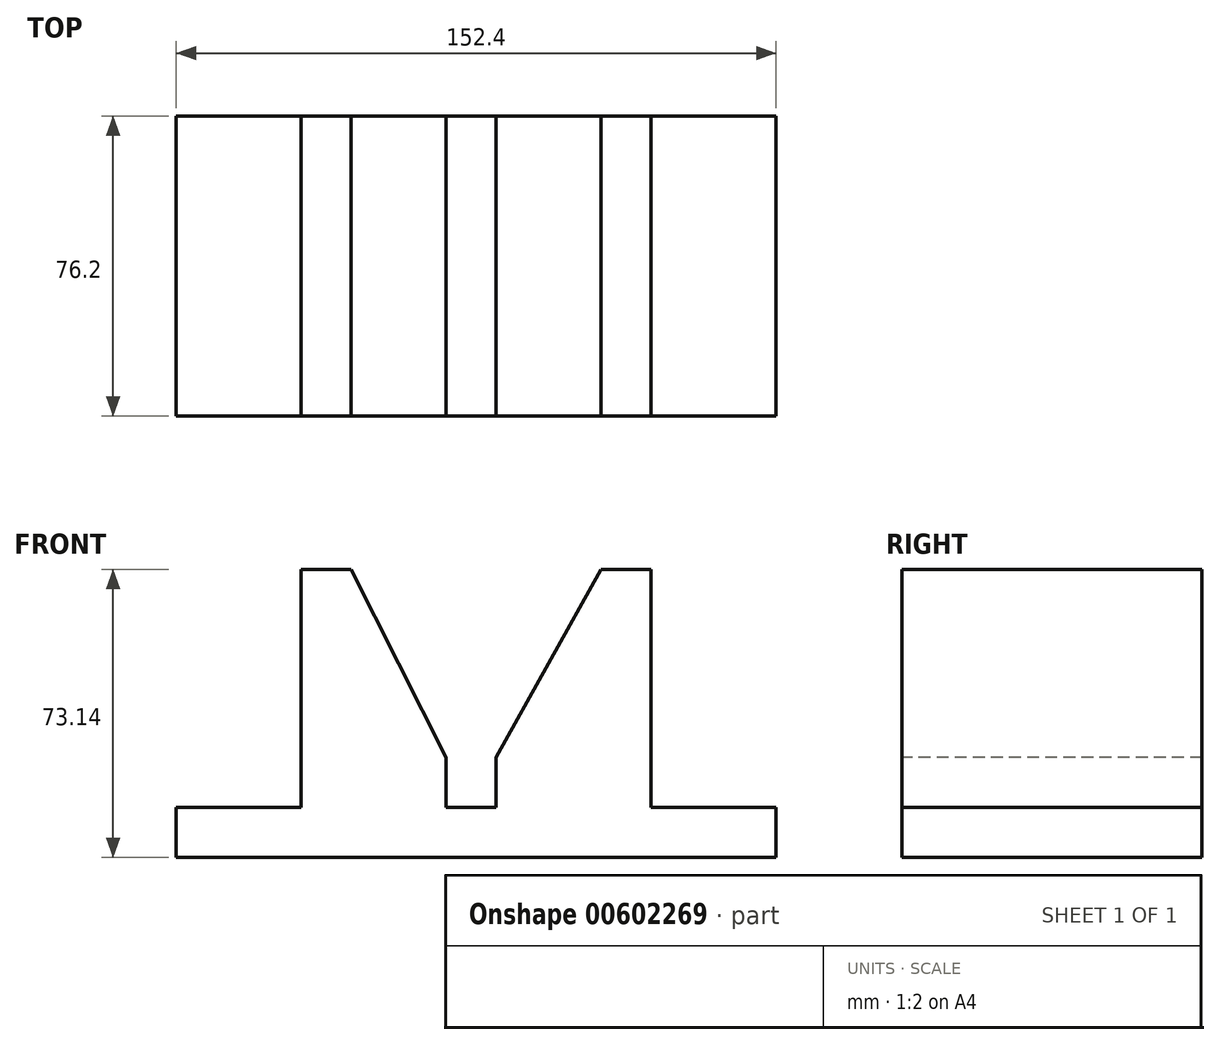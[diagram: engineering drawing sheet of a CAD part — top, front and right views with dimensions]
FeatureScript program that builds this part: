
annotation { "Feature Type Name" : "Feature", "Feature Type Description" : "" }
export const myFeature = defineFeature(function(context is Context, id is Id, definition is map)
    precondition{}
    {
        {
            var Q0;
            Q0=qCreatedBy(makeId("Front.planeOp"),FACE);
            var sketch = newSketch(context, id + "F0", { "sketchPlane" : qUnion([Q0])});
            skLineSegment(sketch, "E0", {"start": v(0, 0) * mm, "end": v(0, 12.7) * mm});
            skLineSegment(sketch, "E1", {"start": v(0, 12.7) * mm, "end": v(31.75, 12.7) * mm});
            skLineSegment(sketch, "E2", {"start": v(31.75, 12.7) * mm, "end": v(31.75, 73.14) * mm});
            skLineSegment(sketch, "E3", {"start": v(31.75, 73.14) * mm, "end": v(44.45, 73.14) * mm});
            skLineSegment(sketch, "E4", {"start": v(44.45, 73.14) * mm, "end": v(68.5, 25.4) * mm});
            skLineSegment(sketch, "E5", {"start": v(68.5, 25.4) * mm, "end": v(68.5, 12.7) * mm});
            skLineSegment(sketch, "E6", {"start": v(68.5, 12.7) * mm, "end": v(81.2, 12.7) * mm});
            skLineSegment(sketch, "E7", {"start": v(81.2, 12.7) * mm, "end": v(81.2, 25.4) * mm});
            skLineSegment(sketch, "E8", {"start": v(81.2, 25.4) * mm, "end": v(107.95, 73.14) * mm});
            skLineSegment(sketch, "E9", {"start": v(107.95, 73.14) * mm, "end": v(120.65, 73.14) * mm});
            skLineSegment(sketch, "E10", {"start": v(120.65, 73.14) * mm, "end": v(120.65, 12.7) * mm});
            skLineSegment(sketch, "E11", {"start": v(120.65, 12.7) * mm, "end": v(152.4, 12.7) * mm});
            skLineSegment(sketch, "E12", {"start": v(152.4, 12.7) * mm, "end": v(152.4, 0) * mm});
            skLineSegment(sketch, "E13", {"start": v(152.4, 0) * mm, "end": v(0, 0) * mm});
            skSolve(sketch);
        }
        {
            var Q0;
            Q0=makeQuery(id+"F0.imprint","IMPRINT",FACE,{"disambiguationData":[TD([[makeQuery(id+"F0.imprint","IMPRINT",EDGE,{"derivedFrom":sQuery(id+"F0.wireOp",EDGE,"E0")}),-1.0]])]});
            extrude(context, id + "F1", {"entities" : qUnion([Q0]), "oppositeDirection" : true, "depth" : 76.2 * mm, "offsetDistance" : 25.4 * mm});
        }
    });
